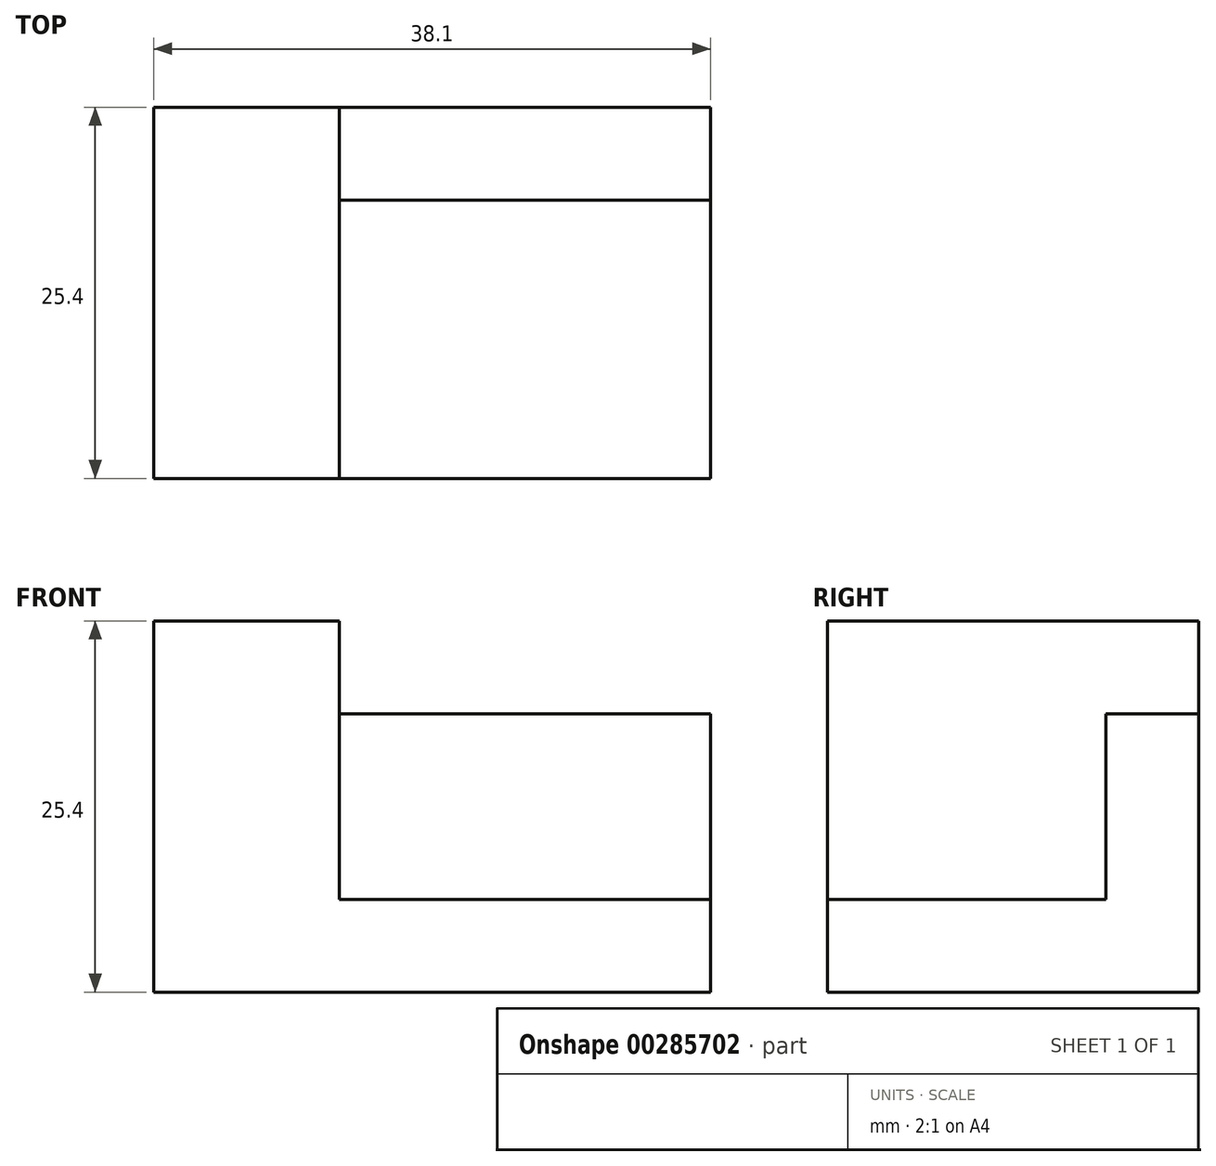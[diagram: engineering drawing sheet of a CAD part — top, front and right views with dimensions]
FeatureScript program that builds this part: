
annotation { "Feature Type Name" : "Feature", "Feature Type Description" : "" }
export const myFeature = defineFeature(function(context is Context, id is Id, definition is map)
    precondition{}
    {
        {
            var Q0;
            Q0=qCreatedBy(makeId("Front.planeOp"),FACE);
            var sketch = newSketch(context, id + "F0", { "sketchPlane" : qUnion([Q0])});
            skLineSegment(sketch, "E0", {"start": v(0, 0) * mm, "end": v(38.1, 0) * mm});
            skLineSegment(sketch, "E1", {"start": v(38.1, 0) * mm, "end": v(38.1, 6.35) * mm});
            skLineSegment(sketch, "E2", {"start": v(38.1, 6.35) * mm, "end": v(12.7, 6.35) * mm});
            skLineSegment(sketch, "E3", {"start": v(0, 0) * mm, "end": v(0, 25.4) * mm});
            skLineSegment(sketch, "E4", {"start": v(0, 25.4) * mm, "end": v(12.7, 25.4) * mm});
            skLineSegment(sketch, "E5", {"start": v(12.7, 25.4) * mm, "end": v(12.7, 6.35) * mm});
            skSolve(sketch);
        }
        {
            var Q0;
            Q0=makeQuery(id+"F0.imprint","IMPRINT",FACE,{"disambiguationData":[TD([[makeQuery(id+"F0.imprint","IMPRINT",EDGE,{"derivedFrom":sQuery(id+"F0.wireOp",EDGE,"E0")}),1.0]])]});
            extrude(context, id + "F1", {"entities" : qUnion([Q0]), "oppositeDirection" : true, "depth" : 25.4 * mm});
        }
        {
            var Q0;
            Q0=makeQuery(id+"F1.opExtrude","SWEPT_FACE",FACE,{"disambiguationData":[OSD([sQuery(id+"F0.wireOp",EDGE,"E2")])]});
            var sketch = newSketch(context, id + "F2", { "sketchPlane" : qUnion([Q0])});
            skLineSegment(sketch, "E6.bottom", {"start": v(12.7, 25.4) * mm, "end": v(38.1, 25.4) * mm});
            skLineSegment(sketch, "E6.top", {"start": v(12.7, 19.05) * mm, "end": v(38.1, 19.05) * mm});
            skLineSegment(sketch, "E6.left", {"start": v(12.7, 25.4) * mm, "end": v(12.7, 19.05) * mm});
            skLineSegment(sketch, "E6.right", {"start": v(38.1, 25.4) * mm, "end": v(38.1, 19.05) * mm});
            skSolve(sketch);
        }
        {
            var Q0;
            Q0 = qSketchRegion(id + "F2", true);
            extrude(context, id + "F3", {"entities" : qUnion([Q0]), "operationType" : NewBodyOperationType.ADD, "depth" : 12.7 * mm});
        }
    });
